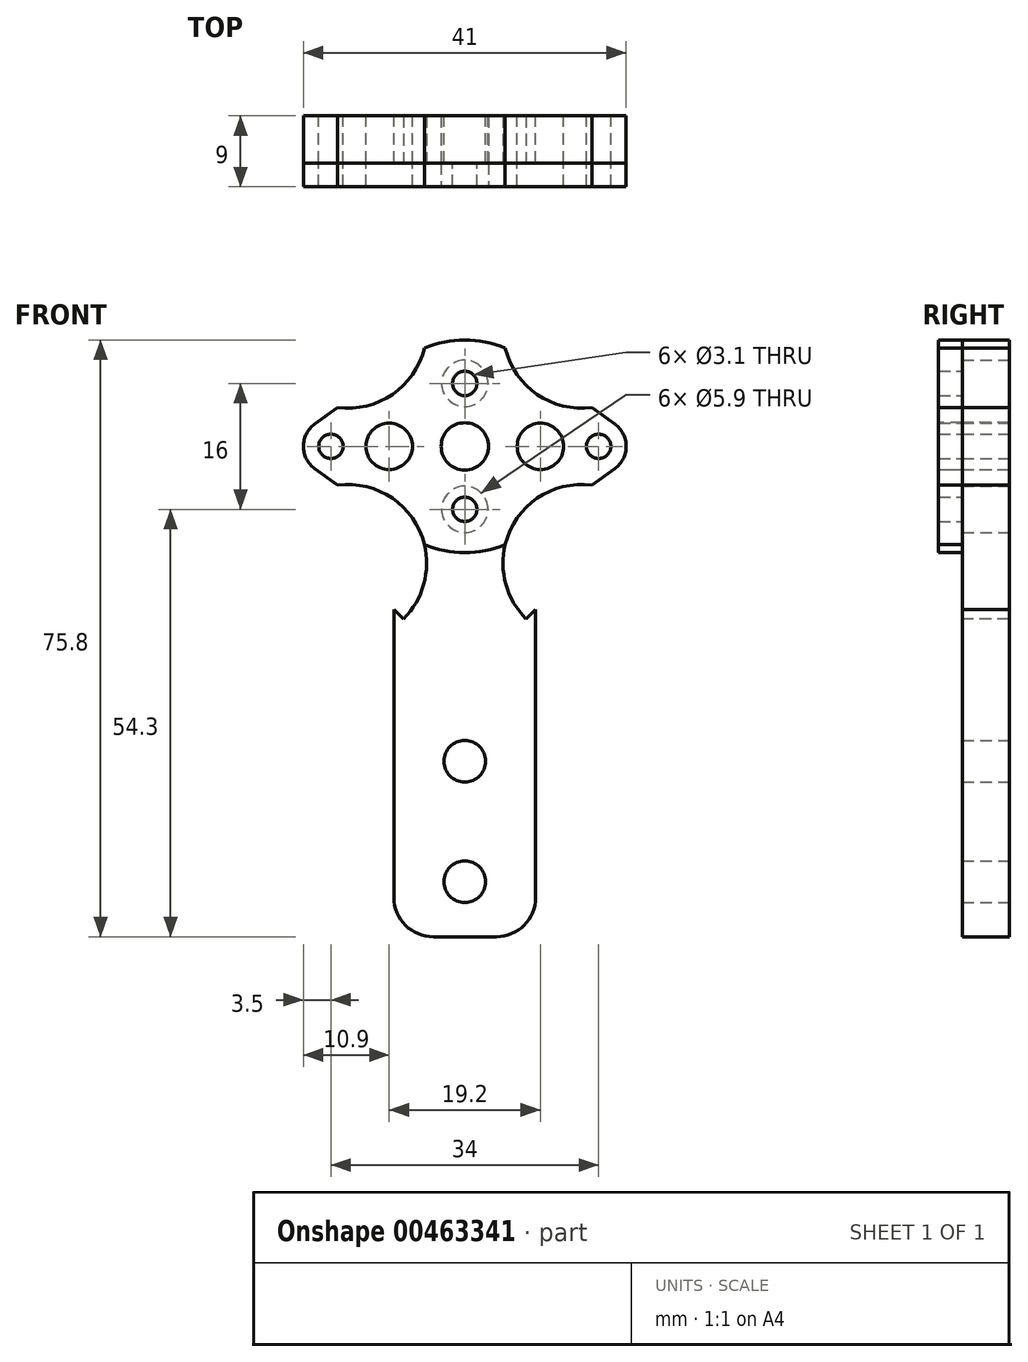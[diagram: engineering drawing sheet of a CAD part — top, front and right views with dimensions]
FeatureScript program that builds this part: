
annotation { "Feature Type Name" : "Feature", "Feature Type Description" : "" }
export const myFeature = defineFeature(function(context is Context, id is Id, definition is map)
    precondition{}
    {
        {
            var Q0;
            Q0=qCreatedBy(makeId("Front.planeOp"),FACE);
            var sketch = newSketch(context, id + "F0", { "sketchPlane" : qUnion([Q0])});
            skCircle(sketch, "E0", {"center": v(0, 0) * mm, "radius": 13.5 * mm});
            skCircle(sketch, "E1", {"center": v(0, 8) * mm, "radius": 1.55 * mm});
            skCircle(sketch, "E2", {"center": v(0, 8) * mm, "radius": 2.95 * mm});
            skLineSegment(sketch, "E3", {"start": v(0, 8) * mm, "end": v(0, 0) * mm});
            skLineSegment(sketch, "E4", {"start": v(0, 0) * mm, "end": v(9.6, 0) * mm});
            skLineSegment(sketch, "E5", {"start": v(0, 0) * mm, "end": v(0, -8) * mm});
            skLineSegment(sketch, "E6", {"start": v(0, 0) * mm, "end": v(-9.6, 0) * mm});
            skLineSegment(sketch, "E7", {"start": v(0, 0) * mm, "end": v(-17, 0) * mm});
            skLineSegment(sketch, "E8", {"start": v(0, 0) * mm, "end": v(17, 0) * mm});
            skCircle(sketch, "E9", {"center": v(-9.6, 0) * mm, "radius": 2.95 * mm});
            skCircle(sketch, "E10", {"center": v(9.6, 0) * mm, "radius": 2.95 * mm});
            skCircle(sketch, "E11", {"center": v(9.6, 0) * mm, "radius": 1.55 * mm});
            skCircle(sketch, "E12", {"center": v(-9.6, 0) * mm, "radius": 1.55 * mm});
            skCircle(sketch, "E13", {"center": v(0, -8) * mm, "radius": 2.95 * mm});
            skCircle(sketch, "E14", {"center": v(0, -8) * mm, "radius": 1.55 * mm});
            skCircle(sketch, "E15", {"center": v(-17, 0) * mm, "radius": 1.55 * mm});
            skCircle(sketch, "E16", {"center": v(17, 0) * mm, "radius": 1.55 * mm});
            skLineSegment(sketch, "E17", {"start": v(-7.94, 10.92) * mm, "end": v(-19.06, 2.83) * mm});
            skLineSegment(sketch, "E18", {"start": v(-19.06, -2.83) * mm, "end": v(-7.94, -10.92) * mm});
            skLineSegment(sketch, "E19", {"start": v(7.94, -10.92) * mm, "end": v(19.06, -2.83) * mm});
            skLineSegment(sketch, "E20", {"start": v(7.94, 10.92) * mm, "end": v(19.06, 2.83) * mm});
            skArc(sketch, "E21", {"start": v(19.06, -2.83) * mm, "mid": v(20.5, 0) * mm, "end": v(19.06, 2.83) * mm});
            skArc(sketch, "E22", {"start": v(-19.06, 2.83) * mm, "mid": v(-20.5, 0) * mm, "end": v(-19.06, -2.83) * mm});
            skLineSegment(sketch, "E23", {"start": v(-9, -10.15) * mm, "end": v(-9, -62.3) * mm});
            skLineSegment(sketch, "E24", {"start": v(-9, -62.3) * mm, "end": v(9, -62.3) * mm});
            skLineSegment(sketch, "E25", {"start": v(9, -62.3) * mm, "end": v(9, -10.15) * mm});
            skCircle(sketch, "E26", {"center": v(0, -40) * mm, "radius": 2.65 * mm});
            skCircle(sketch, "E27", {"center": v(0, -55.3) * mm, "radius": 2.65 * mm});
            skLineSegment(sketch, "E28", {"start": v(0, -62.3) * mm, "end": v(0, -55.3) * mm, "construction": true});
            skSolve(sketch);
        }
        {
            var Q0;
            {var subQ0=sQuery(id+"F0.wireOp",EDGE,"E23");Q0=makeQuery(id+"F0.imprint","IMPRINT",FACE,{"disambiguationData":[TD([[makeQuery(id+"F0.imprint","IMPRINT",EDGE,{"derivedFrom":subQ0}),1.0]])]});}
            var Q1;
            Q1=makeQuery(id+"F0.imprint","IMPRINT",FACE,{"disambiguationData":[TD([[makeQuery(id+"F0.imprint","IMPRINT",EDGE,{"derivedFrom":sQuery(id+"F0.wireOp",EDGE,"E16")}),-1.0]])]});
            var Q2;
            Q2=makeQuery(id+"F0.imprint","IMPRINT",FACE,{"disambiguationData":[TD([[makeQuery(id+"F0.imprint","IMPRINT",EDGE,{"derivedFrom":sQuery(id+"F0.wireOp",EDGE,"E13")}),-1.0]])]});
            var Q3;
            Q3=makeQuery(id+"F0.imprint","IMPRINT",FACE,{"disambiguationData":[TD([[makeQuery(id+"F0.imprint","IMPRINT",EDGE,{"derivedFrom":sQuery(id+"F0.wireOp",EDGE,"E2")}),-1.0]])]});
            var Q4;
            Q4=makeQuery(id+"F0.imprint","IMPRINT",FACE,{"disambiguationData":[TD([[makeQuery(id+"F0.imprint","IMPRINT",EDGE,{"derivedFrom":sQuery(id+"F0.wireOp",EDGE,"E15")}),-1.0]])]});
            extrude(context, id + "F1", {"entities" : qUnion([Q0, Q1, Q2, Q3, Q4]), "endBound" : BoundingType.SYMMETRIC, "depth" : 6 * mm});
        }
        {
            var Q0;
            Q0=makeQuery(id+"F0.imprint","IMPRINT",FACE,{"disambiguationData":[TD([[makeQuery(id+"F0.imprint","IMPRINT",EDGE,{"derivedFrom":sQuery(id+"F0.wireOp",EDGE,"E15")}),-1.0]])]});
            var Q1;
            Q1=makeQuery(id+"F0.imprint","IMPRINT",FACE,{"disambiguationData":[TD([[makeQuery(id+"F0.imprint","IMPRINT",EDGE,{"derivedFrom":sQuery(id+"F0.wireOp",EDGE,"E2")}),-1.0]])]});
            var Q2;
            Q2=makeQuery(id+"F0.imprint","IMPRINT",FACE,{"disambiguationData":[TD([[makeQuery(id+"F0.imprint","IMPRINT",EDGE,{"derivedFrom":sQuery(id+"F0.wireOp",EDGE,"E13")}),-1.0]])]});
            var Q3;
            {var subQ0=sQuery(id+"F0.wireOp",EDGE,"E9");var subQ1=sQuery(id+"F0.wireOp",EDGE,"E7");var subQ2=makeQuery(id+"F0.imprint","INTERSECT",VERTEX,{"disambiguationData":[OD(0.0)],"derivedFrom":[subQ1,subQ0]});Q3=makeQuery(id+"F0.imprint","IMPRINT",FACE,{"disambiguationData":[TD([[makeQuery(id+"F0.imprint","IMPRINT",EDGE,{"disambiguationData":[TD([[subQ2,-1.0]])],"derivedFrom":subQ1}),-1.0]])]});}
            var Q4;
            Q4=makeQuery(id+"F0.imprint","IMPRINT",FACE,{"disambiguationData":[TD([[makeQuery(id+"F0.imprint","IMPRINT",EDGE,{"derivedFrom":sQuery(id+"F0.wireOp",EDGE,"E1")}),-1.0]])]});
            var Q5;
            {var subQ0=sQuery(id+"F0.wireOp",EDGE,"E10");var subQ1=sQuery(id+"F0.wireOp",EDGE,"E8");var subQ2=makeQuery(id+"F0.imprint","INTERSECT",VERTEX,{"disambiguationData":[OD(0.0)],"derivedFrom":[subQ1,subQ0]});Q5=makeQuery(id+"F0.imprint","IMPRINT",FACE,{"disambiguationData":[TD([[makeQuery(id+"F0.imprint","IMPRINT",EDGE,{"disambiguationData":[TD([[subQ2,-1.0]])],"derivedFrom":subQ1}),1.0]])]});}
            var Q6;
            {var subQ0=sQuery(id+"F0.wireOp",EDGE,"E10");var subQ1=sQuery(id+"F0.wireOp",EDGE,"E8");var subQ2=makeQuery(id+"F0.imprint","INTERSECT",VERTEX,{"disambiguationData":[OD(0.0)],"derivedFrom":[subQ1,subQ0]});Q6=makeQuery(id+"F0.imprint","IMPRINT",FACE,{"disambiguationData":[TD([[makeQuery(id+"F0.imprint","IMPRINT",EDGE,{"disambiguationData":[TD([[subQ2,-1.0]])],"derivedFrom":subQ1}),-1.0]])]});}
            var Q7;
            {var subQ0=sQuery(id+"F0.wireOp",EDGE,"E9");var subQ1=sQuery(id+"F0.wireOp",EDGE,"E7");var subQ2=makeQuery(id+"F0.imprint","INTERSECT",VERTEX,{"disambiguationData":[OD(0.0)],"derivedFrom":[subQ1,subQ0]});Q7=makeQuery(id+"F0.imprint","IMPRINT",FACE,{"disambiguationData":[TD([[makeQuery(id+"F0.imprint","IMPRINT",EDGE,{"disambiguationData":[TD([[subQ2,-1.0]])],"derivedFrom":subQ1}),1.0]])]});}
            var Q8;
            Q8=makeQuery(id+"F0.imprint","IMPRINT",FACE,{"disambiguationData":[TD([[makeQuery(id+"F0.imprint","IMPRINT",EDGE,{"derivedFrom":sQuery(id+"F0.wireOp",EDGE,"E13")}),1.0]])]});
            var Q9;
            Q9=makeQuery(id+"F0.imprint","IMPRINT",FACE,{"disambiguationData":[TD([[makeQuery(id+"F0.imprint","IMPRINT",EDGE,{"derivedFrom":sQuery(id+"F0.wireOp",EDGE,"E16")}),-1.0]])]});
            extrude(context, id + "F2", {"entities" : qUnion([Q0, Q1, Q2, Q3, Q4, Q5, Q6, Q7, Q8, Q9]), "depth" : (3 + 3) * mm, "hasSecondDirection" : true, "secondDirectionOppositeDirection" : false, "secondDirectionDepth" : 3 * mm});
        }
        {
            var Q0;
            Q0=makeQuery(id+"F1.opExtrude","SWEPT_EDGE",EDGE,{"disambiguationData":[OSD([sQuery(id+"F0.wireOp",EDGE,"E19"),sQuery(id+"F0.wireOp",EDGE,"E25")])]});
            var Q1;
            Q1=makeQuery(id+"F1.opExtrude","SWEPT_EDGE",EDGE,{"disambiguationData":[OSD([sQuery(id+"F0.wireOp",EDGE,"E18"),sQuery(id+"F0.wireOp",EDGE,"E23")])]});
            fillet(context, id + "F3", {"entities" : qUnion([Q0, Q1]), "radius" : 10 * mm, "tangentPropagation" : true, "allowEdgeOverflow" : false});
        }
        {
            var Q0;
            Q0=makeQuery(id+"F1.opExtrude","SWEPT_EDGE",EDGE,{"disambiguationData":[OSD([sQuery(id+"F0.wireOp",EDGE,"E24"),sQuery(id+"F0.wireOp",EDGE,"E25")])]});
            var Q1;
            Q1=makeQuery(id+"F1.opExtrude","SWEPT_EDGE",EDGE,{"disambiguationData":[OSD([sQuery(id+"F0.wireOp",EDGE,"E23"),sQuery(id+"F0.wireOp",EDGE,"E24")])]});
            fillet(context, id + "F4", {"entities" : qUnion([Q0, Q1]), "radius" : 5 * mm, "tangentPropagation" : true, "allowEdgeOverflow" : false});
        }
        {
            var Q0;
            Q0=makeQuery(id+"F2.opExtrude","CAP_FACE",FACE,{"disambiguationData":[OSD([sQuery(id+"F0.wireOp",EDGE,"E0"),sQuery(id+"F0.wireOp",EDGE,"E1"),sQuery(id+"F0.wireOp",EDGE,"E11"),sQuery(id+"F0.wireOp",EDGE,"E12"),sQuery(id+"F0.wireOp",EDGE,"E14"),sQuery(id+"F0.wireOp",EDGE,"E15"),sQuery(id+"F0.wireOp",EDGE,"E16"),sQuery(id+"F0.wireOp",EDGE,"E17"),sQuery(id+"F0.wireOp",EDGE,"E18"),sQuery(id+"F0.wireOp",EDGE,"E19"),sQuery(id+"F0.wireOp",EDGE,"E20"),sQuery(id+"F0.wireOp",EDGE,"E21"),sQuery(id+"F0.wireOp",EDGE,"E22")])],"isStart":false});
            var sketch = newSketch(context, id + "F5", { "sketchPlane" : qUnion([Q0])});
            skCircle(sketch, "E29", {"center": v(0, 0) * mm, "radius": 3 * mm});
            skArc(sketch, "E30", {"start": v(-21.92, 7.78) * mm, "mid": v(-7.78, 7.78) * mm, "end": v(-7.78, 21.92) * mm});
            skArc(sketch, "E31", {"start": v(7.78, 21.92) * mm, "mid": v(7.78, 7.78) * mm, "end": v(21.92, 7.78) * mm});
            skArc(sketch, "E32", {"start": v(21.92, -7.78) * mm, "mid": v(7.78, -7.78) * mm, "end": v(7.78, -21.92) * mm});
            skArc(sketch, "E33", {"start": v(-7.78, -21.92) * mm, "mid": v(-7.78, -7.78) * mm, "end": v(-21.92, -7.78) * mm});
            skLineSegment(sketch, "E34", {"start": v(0, 0) * mm, "end": v(14.85, 14.85) * mm});
            skLineSegment(sketch, "E35", {"start": v(14.85, -14.85) * mm, "end": v(0, 0) * mm});
            skLineSegment(sketch, "E36", {"start": v(0, 0) * mm, "end": v(-14.85, 14.85) * mm});
            skLineSegment(sketch, "E37", {"start": v(0, 0) * mm, "end": v(-14.85, -14.85) * mm});
            skLineSegment(sketch, "E38", {"start": v(-14.85, -14.85) * mm, "end": v(-21.92, -7.78) * mm});
            skLineSegment(sketch, "E39", {"start": v(14.85, -14.85) * mm, "end": v(7.78, -21.92) * mm});
            skLineSegment(sketch, "E40", {"start": v(14.85, 14.85) * mm, "end": v(21.92, 7.78) * mm});
            skLineSegment(sketch, "E41", {"start": v(-14.85, 14.85) * mm, "end": v(-21.92, 7.78) * mm});
            skLineSegment(sketch, "E42", {"start": v(0, 0) * mm, "end": v(0, 18.56) * mm});
            skLineSegment(sketch, "E43", {"start": v(-7.78, 21.92) * mm, "end": v(-14.85, 14.85) * mm});
            skLineSegment(sketch, "E44", {"start": v(7.78, 21.92) * mm, "end": v(14.85, 14.85) * mm});
            skLineSegment(sketch, "E45", {"start": v(21.92, -7.78) * mm, "end": v(14.85, -14.85) * mm});
            skLineSegment(sketch, "E46", {"start": v(-14.85, -14.85) * mm, "end": v(-7.78, -21.92) * mm});
            skSolve(sketch);
        }
        {
            var Q0;
            {var subQ7=sQuery(id+"F5.wireOp",EDGE,"E43");Q0=makeQuery(id+"F5.imprint","IMPRINT",FACE,{"disambiguationData":[TD([[makeQuery(id+"F5.imprint","IMPRINT",EDGE,{"derivedFrom":subQ7}),1.0]])]});}
            var Q1;
            {var subQ0=sQuery(id+"F5.wireOp",EDGE,"E41");Q1=makeQuery(id+"F5.imprint","IMPRINT",FACE,{"disambiguationData":[TD([[makeQuery(id+"F5.imprint","IMPRINT",EDGE,{"derivedFrom":subQ0}),1.0]])]});}
            var Q2;
            {var subQ0=sQuery(id+"F5.wireOp",EDGE,"E36");var subQ1=sQuery(id+"F5.wireOp",EDGE,"E30");var subQ2=makeQuery(id+"F5.imprint","INTERSECT",VERTEX,{"derivedFrom":[subQ1,subQ0]});Q2=makeQuery(id+"F5.imprint","IMPRINT",FACE,{"disambiguationData":[TD([[makeQuery(id+"F5.imprint","IMPRINT",EDGE,{"disambiguationData":[TD([[subQ2,1.0]])],"derivedFrom":subQ1}),1.0]])]});}
            var Q3;
            {var subQ0=sQuery(id+"F5.wireOp",EDGE,"E36");var subQ1=sQuery(id+"F5.wireOp",EDGE,"E30");var subQ2=makeQuery(id+"F5.imprint","INTERSECT",VERTEX,{"derivedFrom":[subQ1,subQ0]});Q3=makeQuery(id+"F5.imprint","IMPRINT",FACE,{"disambiguationData":[TD([[makeQuery(id+"F5.imprint","IMPRINT",EDGE,{"disambiguationData":[TD([[subQ2,-1.0]])],"derivedFrom":subQ0}),-1.0]])]});}
            var Q4;
            {var subQ0=sQuery(id+"F5.wireOp",EDGE,"E34");var subQ1=sQuery(id+"F5.wireOp",EDGE,"E31");var subQ2=makeQuery(id+"F5.imprint","INTERSECT",VERTEX,{"derivedFrom":[subQ1,subQ0]});Q4=makeQuery(id+"F5.imprint","IMPRINT",FACE,{"disambiguationData":[TD([[makeQuery(id+"F5.imprint","IMPRINT",EDGE,{"disambiguationData":[TD([[subQ2,-1.0]])],"derivedFrom":subQ0}),1.0]])]});}
            var Q5;
            {var subQ0=sQuery(id+"F5.wireOp",EDGE,"E40");Q5=makeQuery(id+"F5.imprint","IMPRINT",FACE,{"disambiguationData":[TD([[makeQuery(id+"F5.imprint","IMPRINT",EDGE,{"derivedFrom":subQ0}),-1.0]])]});}
            var Q6;
            {var subQ0=sQuery(id+"F5.wireOp",EDGE,"E34");var subQ1=sQuery(id+"F5.wireOp",EDGE,"E31");var subQ2=makeQuery(id+"F5.imprint","INTERSECT",VERTEX,{"derivedFrom":[subQ1,subQ0]});Q6=makeQuery(id+"F5.imprint","IMPRINT",FACE,{"disambiguationData":[TD([[makeQuery(id+"F5.imprint","IMPRINT",EDGE,{"disambiguationData":[TD([[subQ2,-1.0]])],"derivedFrom":subQ1}),1.0]])]});}
            var Q7;
            {var subQ0=sQuery(id+"F5.wireOp",EDGE,"E35");var subQ1=sQuery(id+"F5.wireOp",EDGE,"E32");var subQ2=makeQuery(id+"F5.imprint","INTERSECT",VERTEX,{"derivedFrom":[subQ1,subQ0]});Q7=makeQuery(id+"F5.imprint","IMPRINT",FACE,{"disambiguationData":[TD([[makeQuery(id+"F5.imprint","IMPRINT",EDGE,{"disambiguationData":[TD([[subQ2,1.0]])],"derivedFrom":subQ1}),1.0]])]});}
            var Q8;
            {var subQ0=sQuery(id+"F5.wireOp",EDGE,"E45");Q8=makeQuery(id+"F5.imprint","IMPRINT",FACE,{"disambiguationData":[TD([[makeQuery(id+"F5.imprint","IMPRINT",EDGE,{"derivedFrom":subQ0}),-1.0]])]});}
            var Q9;
            {var subQ7=sQuery(id+"F5.wireOp",EDGE,"E39");Q9=makeQuery(id+"F5.imprint","IMPRINT",FACE,{"disambiguationData":[TD([[makeQuery(id+"F5.imprint","IMPRINT",EDGE,{"derivedFrom":subQ7}),-1.0]])]});}
            var Q10;
            {var subQ0=sQuery(id+"F5.wireOp",EDGE,"E35");var subQ1=sQuery(id+"F5.wireOp",EDGE,"E32");var subQ2=makeQuery(id+"F5.imprint","INTERSECT",VERTEX,{"derivedFrom":[subQ1,subQ0]});Q10=makeQuery(id+"F5.imprint","IMPRINT",FACE,{"disambiguationData":[TD([[makeQuery(id+"F5.imprint","IMPRINT",EDGE,{"disambiguationData":[TD([[subQ2,1.0]])],"derivedFrom":subQ0}),1.0]])]});}
            var Q11;
            {var subQ7=sQuery(id+"F5.wireOp",EDGE,"E46");Q11=makeQuery(id+"F5.imprint","IMPRINT",FACE,{"disambiguationData":[TD([[makeQuery(id+"F5.imprint","IMPRINT",EDGE,{"derivedFrom":subQ7}),1.0]])]});}
            var Q12;
            {var subQ0=sQuery(id+"F5.wireOp",EDGE,"E37");var subQ1=sQuery(id+"F5.wireOp",EDGE,"E33");var subQ2=makeQuery(id+"F5.imprint","INTERSECT",VERTEX,{"derivedFrom":[subQ1,subQ0]});Q12=makeQuery(id+"F5.imprint","IMPRINT",FACE,{"disambiguationData":[TD([[makeQuery(id+"F5.imprint","IMPRINT",EDGE,{"disambiguationData":[TD([[subQ2,-1.0]])],"derivedFrom":subQ0}),1.0]])]});}
            var Q13;
            {var subQ0=sQuery(id+"F5.wireOp",EDGE,"E37");var subQ1=sQuery(id+"F5.wireOp",EDGE,"E33");var subQ2=makeQuery(id+"F5.imprint","INTERSECT",VERTEX,{"derivedFrom":[subQ1,subQ0]});Q13=makeQuery(id+"F5.imprint","IMPRINT",FACE,{"disambiguationData":[TD([[makeQuery(id+"F5.imprint","IMPRINT",EDGE,{"disambiguationData":[TD([[subQ2,-1.0]])],"derivedFrom":subQ1}),1.0]])]});}
            var Q14;
            {var subQ0=sQuery(id+"F5.wireOp",EDGE,"E38");Q14=makeQuery(id+"F5.imprint","IMPRINT",FACE,{"disambiguationData":[TD([[makeQuery(id+"F5.imprint","IMPRINT",EDGE,{"derivedFrom":subQ0}),-1.0]])]});}
            var Q15;
            {var subQ7=sQuery(id+"F5.wireOp",EDGE,"E44");Q15=makeQuery(id+"F5.imprint","IMPRINT",FACE,{"disambiguationData":[TD([[makeQuery(id+"F5.imprint","IMPRINT",EDGE,{"derivedFrom":subQ7}),-1.0]])]});}
            var Q16;
            {var subQ0=sQuery(id+"F5.wireOp",EDGE,"E34");var subQ1=sQuery(id+"F5.wireOp",EDGE,"E29");var subQ2=makeQuery(id+"F5.imprint","INTERSECT",VERTEX,{"derivedFrom":[subQ1,subQ0]});Q16=makeQuery(id+"F5.imprint","IMPRINT",FACE,{"disambiguationData":[TD([[makeQuery(id+"F5.imprint","IMPRINT",EDGE,{"disambiguationData":[TD([[subQ2,1.0]])],"derivedFrom":subQ1}),1.0]])]});}
            var Q17;
            {var subQ0=sQuery(id+"F5.wireOp",EDGE,"E42");var subQ1=sQuery(id+"F5.wireOp",EDGE,"E29");var subQ2=makeQuery(id+"F5.imprint","INTERSECT",VERTEX,{"derivedFrom":[subQ1,subQ0]});Q17=makeQuery(id+"F5.imprint","IMPRINT",FACE,{"disambiguationData":[TD([[makeQuery(id+"F5.imprint","IMPRINT",EDGE,{"disambiguationData":[TD([[subQ2,1.0]])],"derivedFrom":subQ1}),1.0]])]});}
            var Q18;
            {var subQ0=sQuery(id+"F5.wireOp",EDGE,"E42");var subQ1=sQuery(id+"F5.wireOp",EDGE,"E29");var subQ2=makeQuery(id+"F5.imprint","INTERSECT",VERTEX,{"derivedFrom":[subQ1,subQ0]});Q18=makeQuery(id+"F5.imprint","IMPRINT",FACE,{"disambiguationData":[TD([[makeQuery(id+"F5.imprint","IMPRINT",EDGE,{"disambiguationData":[TD([[subQ2,-1.0]])],"derivedFrom":subQ1}),1.0]])]});}
            var Q19;
            {var subQ0=sQuery(id+"F5.wireOp",EDGE,"E36");var subQ1=sQuery(id+"F5.wireOp",EDGE,"E29");var subQ2=makeQuery(id+"F5.imprint","INTERSECT",VERTEX,{"derivedFrom":[subQ1,subQ0]});Q19=makeQuery(id+"F5.imprint","IMPRINT",FACE,{"disambiguationData":[TD([[makeQuery(id+"F5.imprint","IMPRINT",EDGE,{"disambiguationData":[TD([[subQ2,-1.0]])],"derivedFrom":subQ1}),1.0]])]});}
            var Q20;
            {var subQ0=sQuery(id+"F5.wireOp",EDGE,"E37");var subQ1=sQuery(id+"F5.wireOp",EDGE,"E29");var subQ2=makeQuery(id+"F5.imprint","INTERSECT",VERTEX,{"derivedFrom":[subQ1,subQ0]});Q20=makeQuery(id+"F5.imprint","IMPRINT",FACE,{"disambiguationData":[TD([[makeQuery(id+"F5.imprint","IMPRINT",EDGE,{"disambiguationData":[TD([[subQ2,-1.0]])],"derivedFrom":subQ1}),1.0]])]});}
            extrude(context, id + "F6", {"entities" : qUnion([Q0, Q1, Q2, Q3, Q4, Q5, Q6, Q7, Q8, Q9, Q10, Q11, Q12, Q13, Q14, Q15, Q16, Q17, Q18, Q19, Q20]), "operationType" : NewBodyOperationType.REMOVE, "oppositeDirection" : true, "depth" : 25 * mm});
        }
    });
